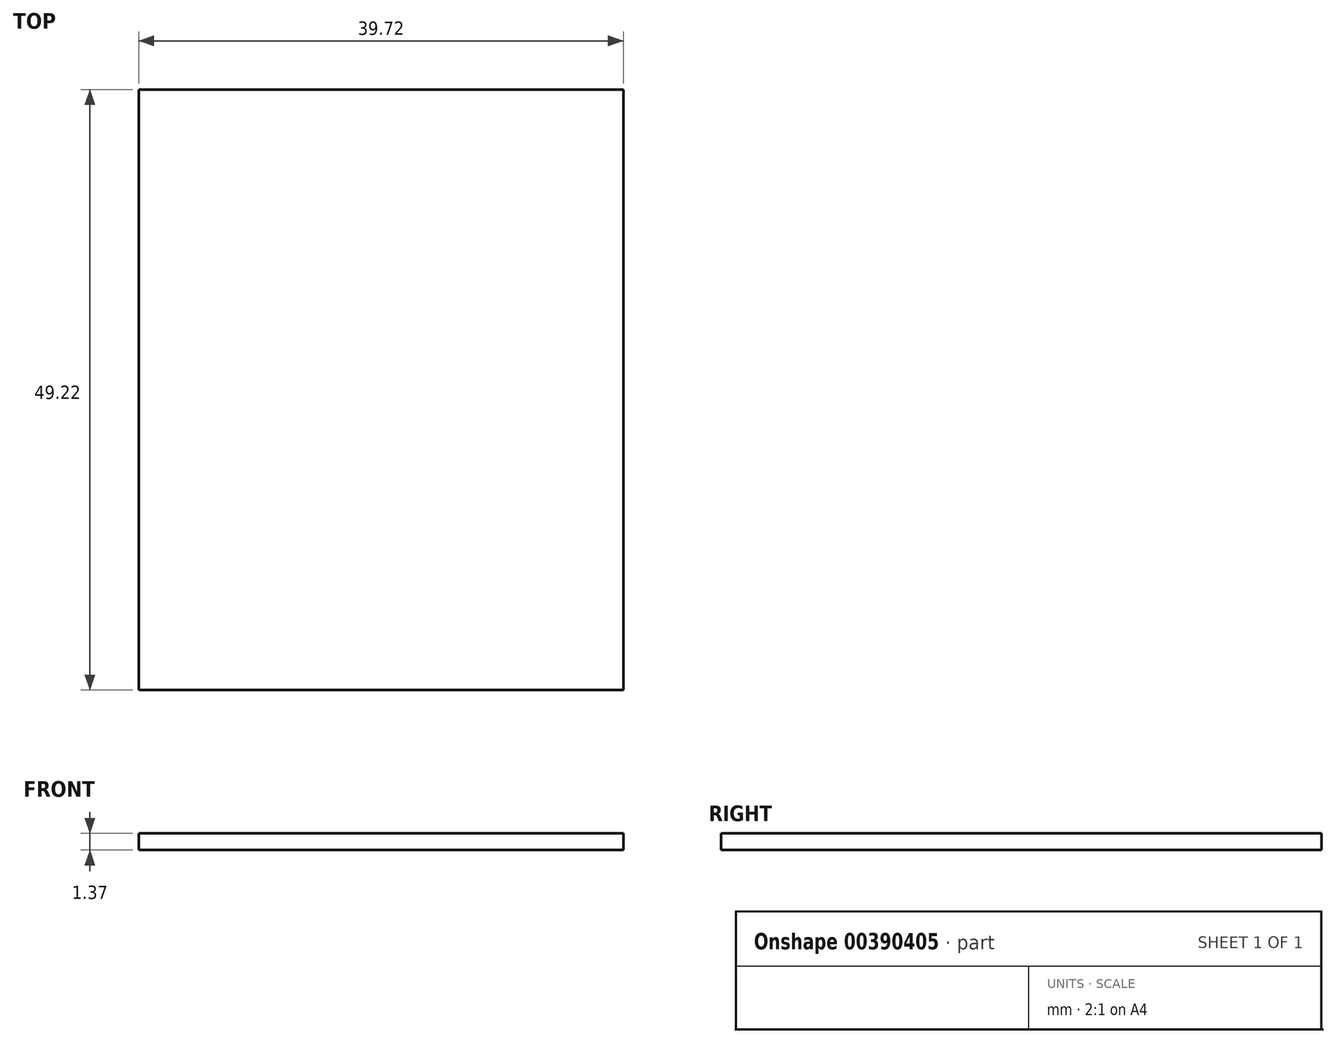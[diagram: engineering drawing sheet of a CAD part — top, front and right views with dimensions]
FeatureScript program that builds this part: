
annotation { "Feature Type Name" : "Feature", "Feature Type Description" : "" }
export const myFeature = defineFeature(function(context is Context, id is Id, definition is map)
    precondition{}
    {
        {
            var Q0;
            Q0=qCreatedBy(makeId("Top.planeOp"),FACE);
            var sketch = newSketch(context, id + "F0", { "sketchPlane" : qUnion([Q0])});
            skLineSegment(sketch, "E0.bottom", {"start": v(19.86, -24.6) * mm, "end": v(-19.85, -24.61) * mm});
            skLineSegment(sketch, "E0.top", {"start": v(19.85, 24.61) * mm, "end": v(-19.86, 24.6) * mm});
            skLineSegment(sketch, "E0.left", {"start": v(19.86, -24.6) * mm, "end": v(19.85, 24.61) * mm});
            skLineSegment(sketch, "E0.right", {"start": v(-19.85, -24.61) * mm, "end": v(-19.86, 24.6) * mm});
            skPoint(sketch, "E0.middle", {"position": v(0, 0) * mm});
            skSolve(sketch);
        }
        {
            var Q0;
            Q0 = qSketchRegion(id + "F0", true);
            var Q1;
            Q1=makeQuery(id+"F0.imprint","IMPRINT",FACE,{"disambiguationData":[TD([[makeQuery(id+"F0.imprint","IMPRINT",EDGE,{"derivedFrom":sQuery(id+"F0.wireOp",EDGE,"E0.bottom")}),-1.0]])]});
            extrude(context, id + "F1", {"entities" : qUnion([Q0, Q1]), "depth" : 1.37 * mm});
        }
    });
